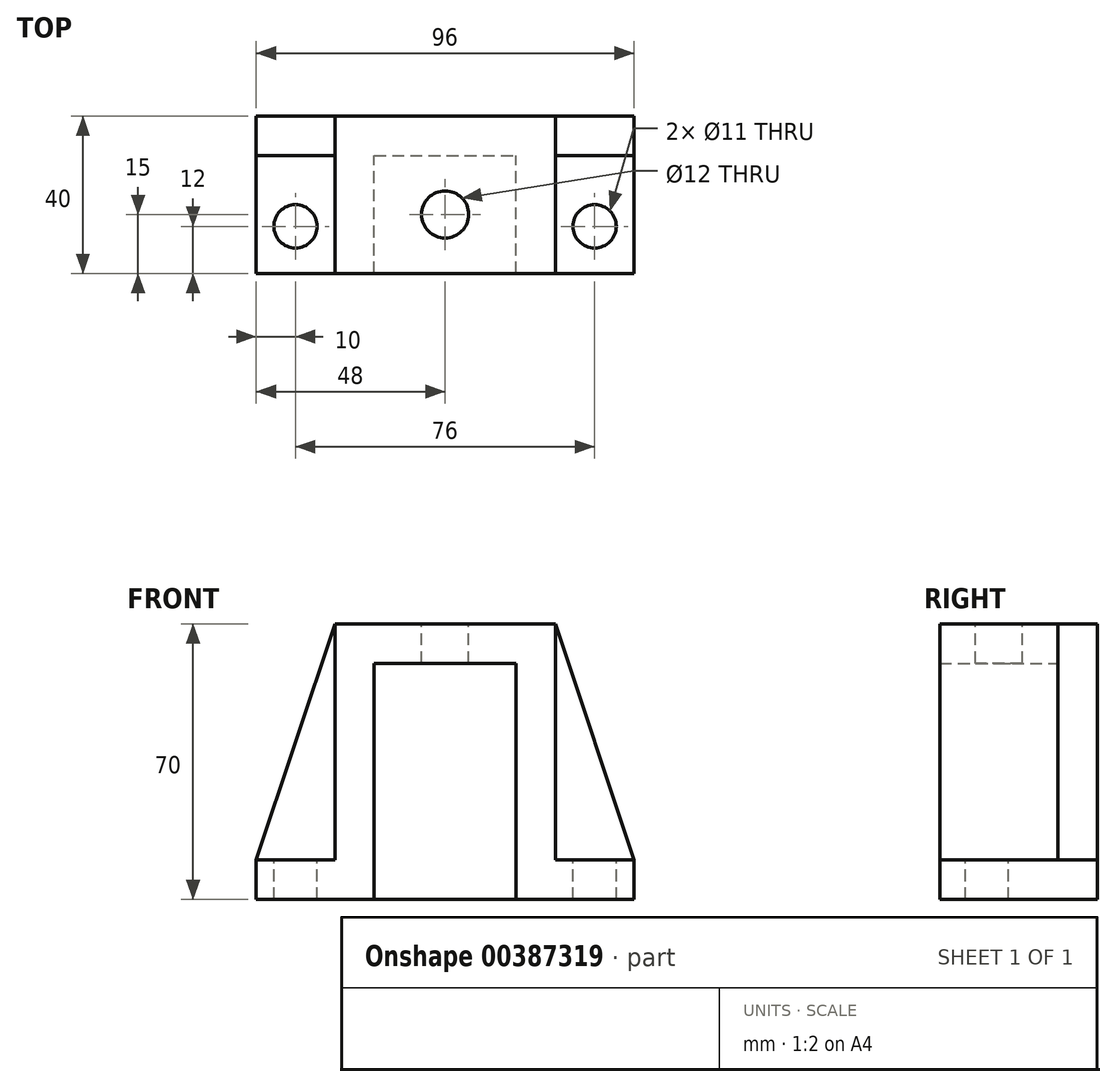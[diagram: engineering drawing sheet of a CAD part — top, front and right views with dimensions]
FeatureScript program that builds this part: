
annotation { "Feature Type Name" : "Feature", "Feature Type Description" : "" }
export const myFeature = defineFeature(function(context is Context, id is Id, definition is map)
    precondition{}
    {
        {
            var Q0;
            Q0=qCreatedBy(makeId("Front.planeOp"),FACE);
            var sketch = newSketch(context, id + "F0", { "sketchPlane" : qUnion([Q0])});
            skLineSegment(sketch, "E0", {"start": v(-48, -35) * mm, "end": v(48, -35) * mm});
            skLineSegment(sketch, "E1", {"start": v(48, -35) * mm, "end": v(48, -25) * mm});
            skLineSegment(sketch, "E2", {"start": v(48, -25) * mm, "end": v(28, -25) * mm});
            skLineSegment(sketch, "E3", {"start": v(28, -25) * mm, "end": v(28, 35) * mm});
            skLineSegment(sketch, "E4", {"start": v(28, 35) * mm, "end": v(-28, 35) * mm});
            skLineSegment(sketch, "E5", {"start": v(-28, 35) * mm, "end": v(-28, -25) * mm});
            skLineSegment(sketch, "E6", {"start": v(-28, -25) * mm, "end": v(-48, -25) * mm});
            skLineSegment(sketch, "E7", {"start": v(-48, -25) * mm, "end": v(-48, -35) * mm});
            skLineSegment(sketch, "E8", {"start": v(-48, -25) * mm, "end": v(-28, 35) * mm});
            skLineSegment(sketch, "E9", {"start": v(28, 35) * mm, "end": v(48, -25) * mm});
            skLineSegment(sketch, "E10", {"start": v(-18, -35) * mm, "end": v(-18, 25) * mm});
            skLineSegment(sketch, "E11", {"start": v(-18, 25) * mm, "end": v(18, 25) * mm});
            skLineSegment(sketch, "E12", {"start": v(18, 25) * mm, "end": v(18, -35) * mm});
            skSolve(sketch);
        }
        {
            var Q0;
            {var subQ3=sQuery(id+"F0.wireOp",EDGE,"E1");Q0=makeQuery(id+"F0.imprint","IMPRINT",FACE,{"disambiguationData":[TD([[makeQuery(id+"F0.imprint","IMPRINT",EDGE,{"derivedFrom":subQ3}),1.0]])]});}
            extrude(context, id + "F1", {"entities" : qUnion([Q0]), "depth" : 40 * mm});
        }
        {
            var Q0;
            Q0 = qSketchRegion(id + "F0", true);
            extrude(context, id + "F2", {"entities" : qUnion([Q0]), "operationType" : NewBodyOperationType.ADD, "depth" : 10 * mm});
        }
        {
            var Q0;
            Q0=makeQuery(id+"F1.opExtrude","SWEPT_FACE",FACE,{"disambiguationData":[OSD([sQuery(id+"F0.wireOp",EDGE,"E4")])]});
            var sketch = newSketch(context, id + "F3", { "sketchPlane" : qUnion([Q0])});
            skCircle(sketch, "E13", {"center": v(0, -25) * mm, "radius": 6 * mm});
            skSolve(sketch);
        }
        {
            var Q0;
            Q0=makeQuery(id+"F1.opExtrude","SWEPT_FACE",FACE,{"disambiguationData":[OSD([sQuery(id+"F0.wireOp",EDGE,"E6")])]});
            var sketch = newSketch(context, id + "F4", { "sketchPlane" : qUnion([Q0])});
            skCircle(sketch, "E14", {"center": v(-38, -28) * mm, "radius": 5.5 * mm});
            skCircle(sketch, "E15", {"center": v(38, -28) * mm, "radius": 5.5 * mm});
            skSolve(sketch);
        }
        {
            var Q0;
            Q0=makeQuery(id+"F4.imprint","IMPRINT",FACE,{"disambiguationData":[TD([[makeQuery(id+"F4.imprint","IMPRINT",EDGE,{"derivedFrom":sQuery(id+"F4.wireOp",EDGE,"E14")}),1.0]])]});
            var Q1;
            Q1=makeQuery(id+"F3.imprint","IMPRINT",FACE,{"disambiguationData":[TD([[makeQuery(id+"F3.imprint","IMPRINT",EDGE,{"derivedFrom":sQuery(id+"F3.wireOp",EDGE,"E13")}),1.0]])]});
            var Q2;
            Q2=makeQuery(id+"F4.imprint","IMPRINT",FACE,{"disambiguationData":[TD([[makeQuery(id+"F4.imprint","IMPRINT",EDGE,{"derivedFrom":sQuery(id+"F4.wireOp",EDGE,"E15")}),1.0]])]});
            extrude(context, id + "F5", {"entities" : qUnion([Q0, Q1, Q2]), "operationType" : NewBodyOperationType.REMOVE, "oppositeDirection" : true, "depth" : 25 * mm});
        }
    });
